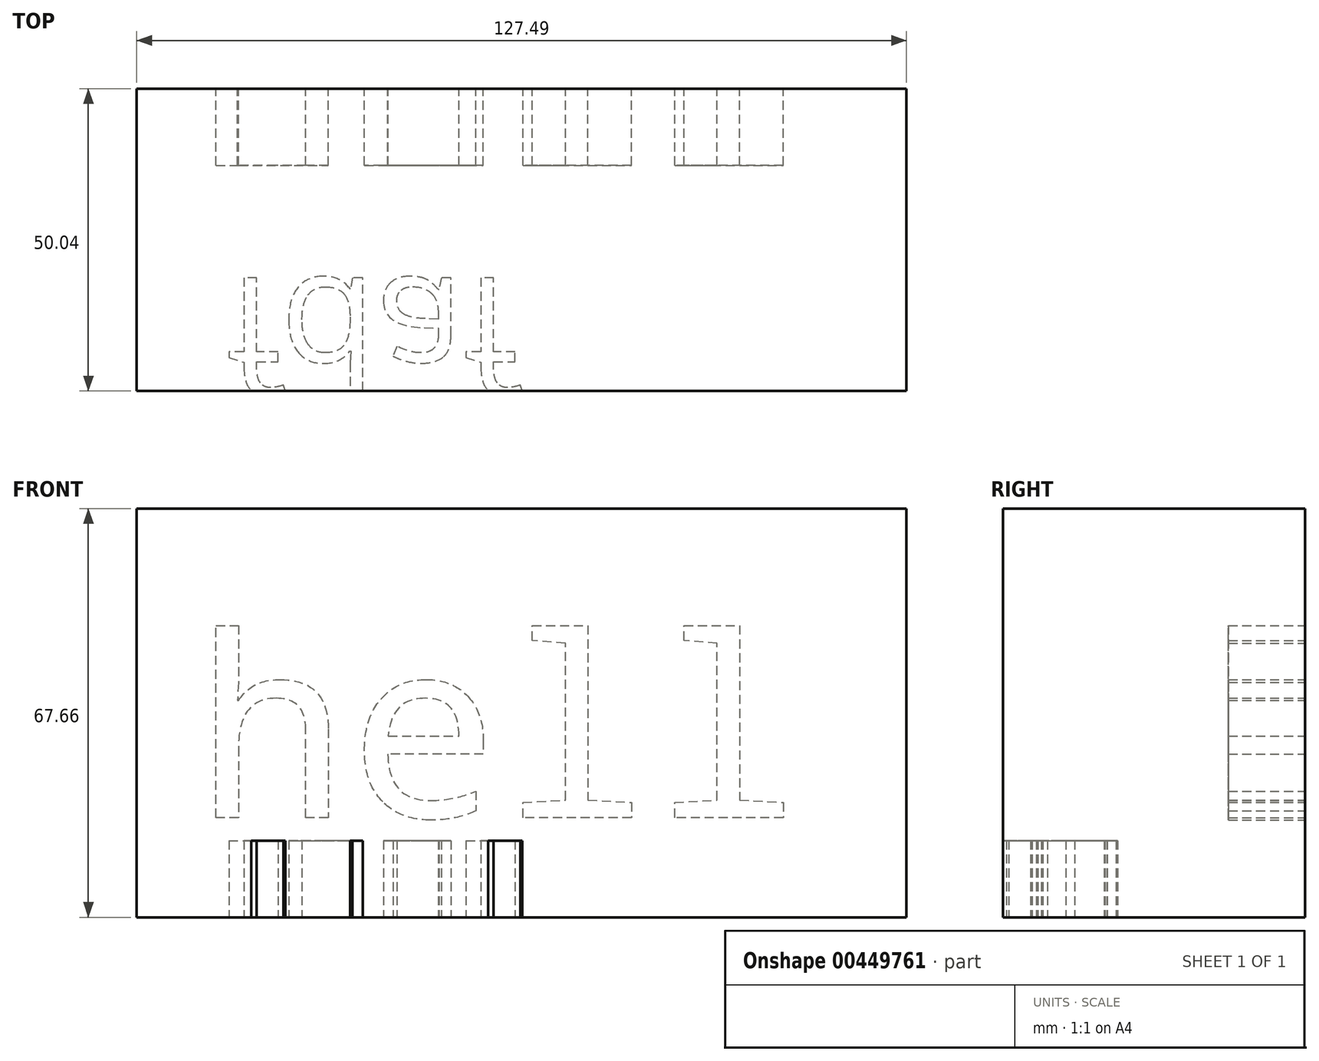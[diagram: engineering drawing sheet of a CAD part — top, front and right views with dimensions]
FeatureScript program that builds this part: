
annotation { "Feature Type Name" : "Feature", "Feature Type Description" : "" }
export const myFeature = defineFeature(function(context is Context, id is Id, definition is map)
    precondition{}
    {
        {
            var Q0;
            Q0=qCreatedBy(makeId("Front.planeOp"),FACE);
            var sketch = newSketch(context, id + "F0", { "sketchPlane" : qUnion([Q0])});
            skLineSegment(sketch, "E0.bottom", {"start": v(-65.76, 32.76) * mm, "end": v(61.73, 32.76) * mm});
            skLineSegment(sketch, "E0.top", {"start": v(-65.76, -34.9) * mm, "end": v(61.73, -34.9) * mm});
            skLineSegment(sketch, "E0.left", {"start": v(-65.76, 32.76) * mm, "end": v(-65.76, -34.9) * mm});
            skLineSegment(sketch, "E0.right", {"start": v(61.73, 32.76) * mm, "end": v(61.73, -34.9) * mm});
            skSolve(sketch);
        }
        {
            var Q0;
            Q0 = qSketchRegion(id + "F0", true);
            extrude(context, id + "F1", {"entities" : qUnion([Q0]), "depth" : 50.04 * mm});
        }
        {
            var Q0;
            Q0=qCreatedBy(makeId("Front.planeOp"),FACE);
            var sketch = newSketch(context, id + "F2", { "sketchPlane" : qUnion([Q0])});
            skText(sketch, "E1", { "text": "hell", "fontName": "DroidSansMono.ttf"});
            const initialGuessF2  = {"E1": [-0.0559, -0.0184, 1, 0, 0.03015]};
            skSetInitialGuess(sketch, initialGuessF2);
            skSolve(sketch);
        }
        {
            var Q0;
            Q0 = qSketchRegion(id + "F2", true);
            extrude(context, id + "F3", {"entities" : qUnion([Q0]), "operationType" : NewBodyOperationType.REMOVE, "depth" : 12.7 * mm});
        }
        {
            var Q0;
            Q0=makeQuery(id+"F1.opExtrude","SWEPT_FACE",FACE,{"disambiguationData":[OSD([sQuery(id+"F0.wireOp",EDGE,"E0.top")])]});
            var sketch = newSketch(context, id + "F4", { "sketchPlane" : qUnion([Q0])});
            skText(sketch, "E2", { "text": "fdaf", "fontName": "OpenSans-Regular.ttf"});
            const initialGuessF4  = {"E2": [-0.05086, 0.0313, 1, 0, 0.01874]};
            skSetInitialGuess(sketch, initialGuessF4);
            skSolve(sketch);
        }
        {
            var Q0;
            Q0 = qSketchRegion(id + "F4", true);
            extrude(context, id + "F5", {"entities" : qUnion([Q0]), "operationType" : NewBodyOperationType.REMOVE, "oppositeDirection" : true, "depth" : 12.7 * mm});
        }
    });
